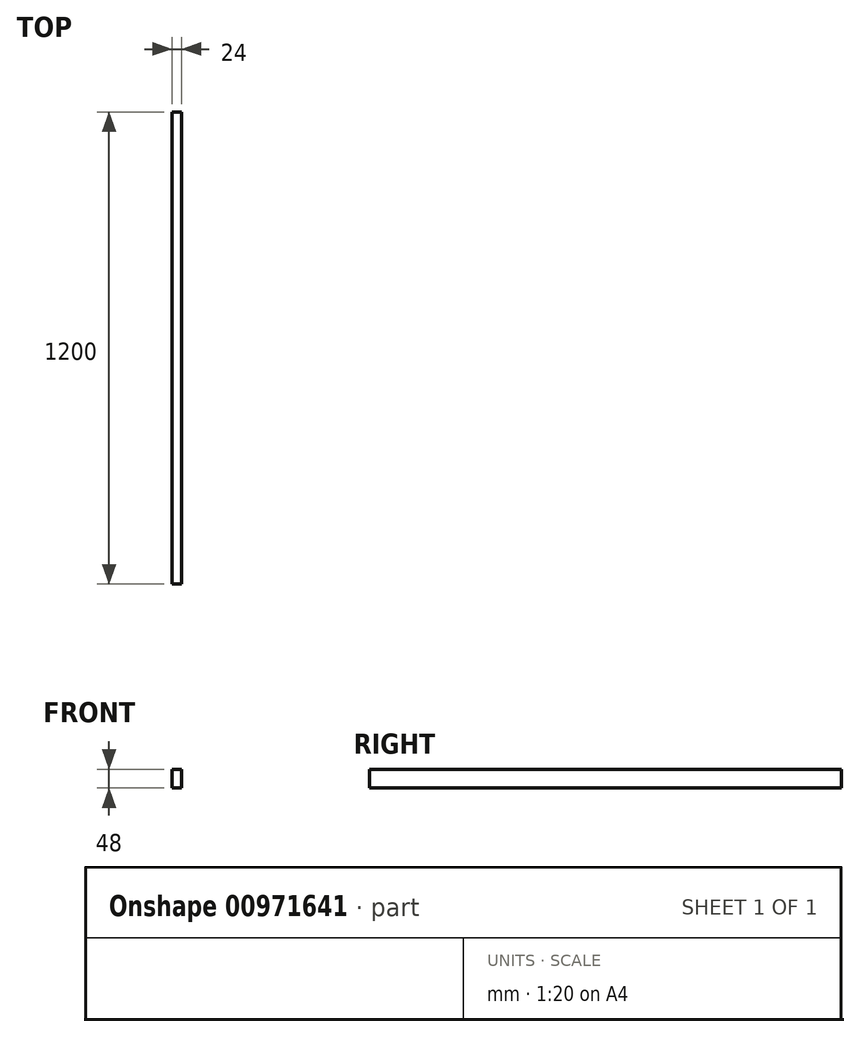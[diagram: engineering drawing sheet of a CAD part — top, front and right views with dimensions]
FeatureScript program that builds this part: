
annotation { "Feature Type Name" : "Feature", "Feature Type Description" : "" }
export const myFeature = defineFeature(function(context is Context, id is Id, definition is map)
    precondition{}
    {
        {
            assignVariable(context, id + "F0", {"name" : "c", "anyValue" : 1200});
        }
        {
            var Q0;
            Q0=qCreatedBy(makeId("Front.planeOp"),FACE);
            var sketch = newSketch(context, id + "F1", { "sketchPlane" : qUnion([Q0])});
            skLineSegment(sketch, "E0.bottom", {"start": v(12, -24) * mm, "end": v(-12, -24) * mm});
            skLineSegment(sketch, "E0.top", {"start": v(12, 24) * mm, "end": v(-12, 24) * mm});
            skLineSegment(sketch, "E0.left", {"start": v(12, -24) * mm, "end": v(12, 24) * mm});
            skLineSegment(sketch, "E0.right", {"start": v(-12, -24) * mm, "end": v(-12, 24) * mm});
            skPoint(sketch, "E0.middle", {"position": v(0, 0) * mm});
            skSolve(sketch);
        }
        {
            var Q0;
            Q0=qSketchRegion(id+"F1",true);
            var Q1;
            Q1=makeQuery(id+"F1.imprint","IMPRINT",FACE,{"disambiguationData":[TD([[makeQuery(id+"F1.imprint","IMPRINT",EDGE,{"derivedFrom":sQuery(id+"F1.wireOp",EDGE,"E0.bottom")}),-1.0]])]});
            extrude(context, id + "F2", {"entities" : qUnion([Q0, Q1]), "depth" : (getVariable(context, 'c')) * mm, "offsetDistance" : 25 * mm});
        }
    });
